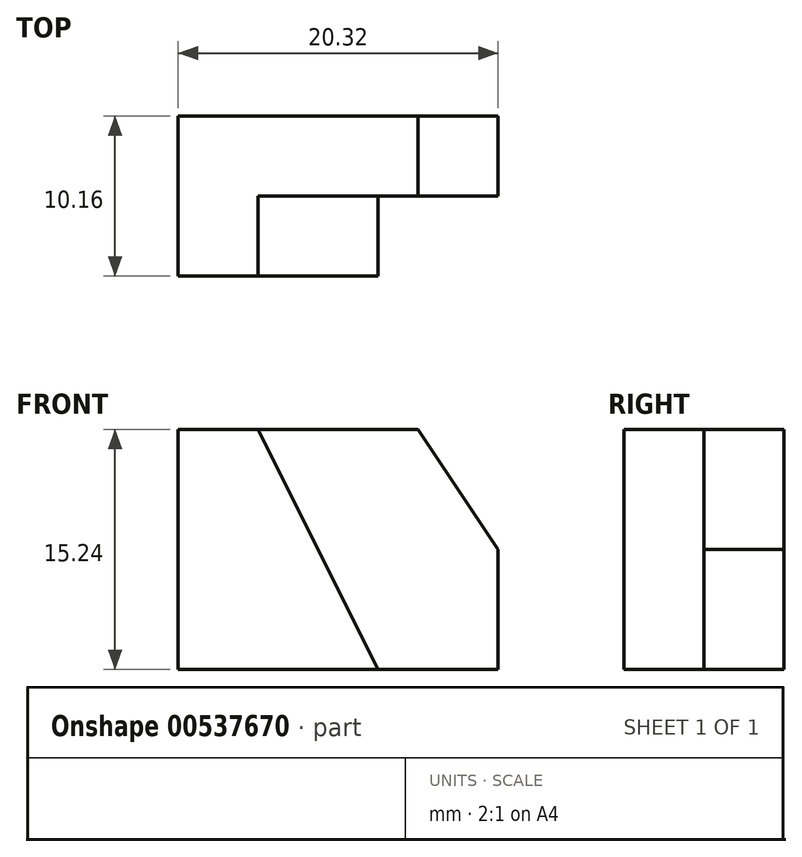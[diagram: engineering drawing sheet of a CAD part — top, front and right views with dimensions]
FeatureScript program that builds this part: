
annotation { "Feature Type Name" : "Feature", "Feature Type Description" : "" }
export const myFeature = defineFeature(function(context is Context, id is Id, definition is map)
    precondition{}
    {
        {
            var Q0;
            Q0=qCreatedBy(makeId("Front.planeOp"),FACE);
            var sketch = newSketch(context, id + "F0", { "sketchPlane" : qUnion([Q0])});
            skLineSegment(sketch, "E0", {"start": v(0, 0) * mm, "end": v(12.7, 0) * mm});
            skLineSegment(sketch, "E1", {"start": v(0, 0) * mm, "end": v(0, 15.24) * mm});
            skLineSegment(sketch, "E2", {"start": v(0, 15.24) * mm, "end": v(5.08, 15.24) * mm});
            skLineSegment(sketch, "E3", {"start": v(5.08, 15.24) * mm, "end": v(12.7, 0) * mm});
            skSolve(sketch);
        }
        {
            var Q0;
            Q0=qSketchRegion(id+"F0",true);
            extrude(context, id + "F1", {"entities" : qUnion([Q0]), "depth" : 5.08 * mm, "offsetDistance" : 25.4 * mm});
        }
        {
            var Q0;
            Q0=makeQuery(id+"F1.opExtrude","CAP_FACE",FACE,{"disambiguationData":[OSD([sQuery(id+"F0.wireOp",EDGE,"E0"),sQuery(id+"F0.wireOp",EDGE,"E1"),sQuery(id+"F0.wireOp",EDGE,"E2"),sQuery(id+"F0.wireOp",EDGE,"E3")])],"isStart":true});
            var sketch = newSketch(context, id + "F2", { "sketchPlane" : qUnion([Q0])});
            skLineSegment(sketch, "E4", {"start": v(0, 0) * mm, "end": v(-20.32, 0) * mm});
            skLineSegment(sketch, "E5", {"start": v(-20.32, 0) * mm, "end": v(-20.32, 7.62) * mm});
            skLineSegment(sketch, "E6", {"start": v(0, 15.24) * mm, "end": v(-15.24, 15.24) * mm});
            skLineSegment(sketch, "E7", {"start": v(-15.24, 15.24) * mm, "end": v(-20.32, 7.62) * mm});
            skSolve(sketch);
        }
        {
            var Q0;
            Q0=qSketchRegion(id+"F2",true);
            var Q1;
            {var subQ1=makeQuery(id+"F1.opExtrude","CAP_EDGE",EDGE,{"disambiguationData":[OSD([sQuery(id+"F0.wireOp",EDGE,"E1")])],"isStart":true});Q1=makeQuery(id+"F2.imprint","IMPRINT",FACE,{"disambiguationData":[TD([[makeQuery(id+"F2.imprint","IMPRINT",EDGE,{"derivedFrom":subQ1}),1.0]])]});}
            var Q2;
            {var subQ3=sQuery(id+"F2.wireOp",EDGE,"E5");Q2=makeQuery(id+"F2.imprint","IMPRINT",FACE,{"disambiguationData":[TD([[makeQuery(id+"F2.imprint","IMPRINT",EDGE,{"derivedFrom":subQ3}),-1.0]])]});}
            extrude(context, id + "F3", {"entities" : qUnion([Q0, Q1, Q2]), "operationType" : NewBodyOperationType.ADD, "depth" : 5.08 * mm, "offsetDistance" : 25.4 * mm});
        }
    });
